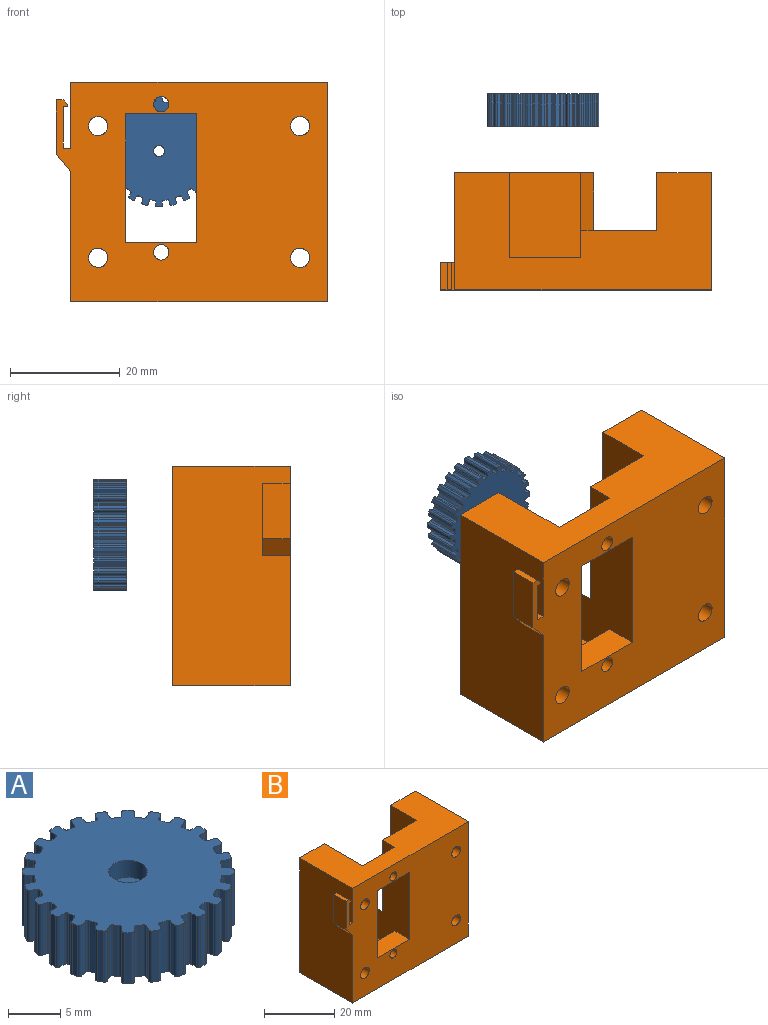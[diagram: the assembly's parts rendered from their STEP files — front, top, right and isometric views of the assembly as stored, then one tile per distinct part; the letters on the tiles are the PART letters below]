
ASSEMBLY  parts=2 mates=1
PART A: 197 faces, bbox 20.4x20.4x6 mm
  f0: cylinder r=1mm len=4mm, axis (0,0,1), area 25.1mm2, adj f194,f196
  f1: cylinder r=0.3mm len=6mm, axis (0,0,-1), area 2.7mm2, adj f2,f192,f193,f194
  f2: cylinder r=9mm len=6mm, axis (0,0,-1), area 3.7mm2, adj f1,f3,f193,f194
  f3: cylinder r=0.3mm len=6mm, axis (0,0,-1), area 2.7mm2, adj f2,f4,f193,f194
  f4: plane 6x0.54mm, normal (0.5,-0.87,0), area 3.7mm2, adj f3,f5,f193,f194
  f5: cylinder r=0.3mm len=6mm, axis (0,0,-1), area 2.8mm2, adj f4,f6,f193,f194
  f6: plane 6x0.52mm, normal (0.87,0.5,0), area 3.6mm2, adj f5,f7,f193,f194
  f7: cylinder r=0.3mm len=6mm, axis (0,0,-1), area 2.8mm2, adj f6,f8,f193,f194
  f8: plane 6x0.54mm, normal (-0.5,0.87,0), area 3.7mm2, adj f7,f9,f193,f194
  f9: cylinder r=0.3mm len=6mm, axis (0,0,-1), area 2.7mm2, adj f8,f10,f193,f194
  f10: cylinder r=9mm len=6mm, axis (0,0,-1), area 3.7mm2, adj f9,f11,f193,f194
  f11: cylinder r=0.3mm len=6mm, axis (0,0,-1), area 2.7mm2, adj f10,f12,f193,f194
  f12: plane 6x0.44mm, normal (0.71,-0.71,0), area 3.7mm2, adj f11,f13,f193,f194
  f13: cylinder r=0.3mm len=6mm, axis (0,0,-1), area 2.8mm2, adj f12,f14,f193,f194
  f14: plane 6x0.42mm, normal (0.71,0.71,0), area 3.6mm2, adj f13,f15,f193,f194
  f15: cylinder r=0.3mm len=6mm, axis (0,0,-1), area 2.8mm2, adj f14,f16,f193,f194
  f16: plane 6x0.44mm, normal (-0.71,0.71,0), area 3.7mm2, adj f15,f17,f193,f194
  f17: cylinder r=0.3mm len=6mm, axis (0,0,-1), area 2.7mm2, adj f16,f18,f193,f194
  f18: cylinder r=9mm len=6mm, axis (0,0,-1), area 3.7mm2, adj f17,f19,f193,f194
  f19: cylinder r=0.3mm len=6mm, axis (0,0,-1), area 2.7mm2, adj f18,f20,f193,f194
  f20: plane 6x0.54mm, normal (0.87,-0.5,0), area 3.7mm2, adj f19,f21,f193,f194
  f21: cylinder r=0.3mm len=6mm, axis (0,0,-1), area 2.8mm2, adj f20,f22,f193,f194
  f22: plane 6x0.52mm, normal (0.5,0.87,0), area 3.6mm2, adj f21,f23,f193,f194
  f23: cylinder r=0.3mm len=6mm, axis (0,0,-1), area 2.8mm2, adj f22,f24,f193,f194
  f24: plane 6x0.54mm, normal (-0.87,0.5,0), area 3.7mm2, adj f23,f25,f193,f194
  f25: cylinder r=0.3mm len=6mm, axis (0,0,-1), area 2.7mm2, adj f24,f26,f193,f194
  f26: cylinder r=9mm len=6mm, axis (0,0,-1), area 3.7mm2, adj f25,f27,f193,f194
  f27: cylinder r=0.3mm len=6mm, axis (0,0,-1), area 2.7mm2, adj f26,f28,f193,f194
  f28: plane 6x0.6mm, normal (0.97,-0.26,0), area 3.7mm2, adj f27,f29,f193,f194
  f29: cylinder r=0.3mm len=6mm, axis (0,0,-1), area 2.8mm2, adj f28,f30,f193,f194
  f30: plane 6x0.58mm, normal (0.26,0.97,0), area 3.6mm2, adj f29,f31,f193,f194
  f31: cylinder r=0.3mm len=6mm, axis (0,0,-1), area 2.8mm2, adj f30,f32,f193,f194
  f32: plane 6x0.6mm, normal (-0.97,0.26,0), area 3.7mm2, adj f31,f33,f193,f194
  f33: cylinder r=0.3mm len=6mm, axis (0,0,-1), area 2.7mm2, adj f32,f34,f193,f194
  f34: cylinder r=9mm len=6mm, axis (0,0,-1), area 3.7mm2, adj f33,f35,f193,f194
  f35: cylinder r=0.3mm len=6mm, axis (0,0,-1), area 2.7mm2, adj f34,f36,f193,f194
  f36: plane 6x0.62mm, normal (1,0,0), area 3.7mm2, adj f35,f37,f193,f194
  f37: cylinder r=0.3mm len=6mm, axis (0,0,-1), area 2.8mm2, adj f36,f38,f193,f194
  f38: plane 6x0.6mm, normal (0,1,0), area 3.6mm2, adj f37,f39,f193,f194
  f39: cylinder r=0.3mm len=6mm, axis (0,0,-1), area 2.8mm2, adj f38,f40,f193,f194
  f40: plane 6x0.62mm, normal (-1,0,0), area 3.7mm2, adj f39,f41,f193,f194
  f41: cylinder r=0.3mm len=6mm, axis (0,0,-1), area 2.7mm2, adj f40,f42,f193,f194
  f42: cylinder r=9mm len=6mm, axis (0,0,-1), area 3.7mm2, adj f41,f43,f193,f194
  f43: cylinder r=0.3mm len=6mm, axis (0,0,-1), area 2.7mm2, adj f42,f44,f193,f194
  f44: plane 6x0.6mm, normal (0.97,0.26,0), area 3.7mm2, adj f43,f45,f193,f194
  f45: cylinder r=0.3mm len=6mm, axis (0,0,-1), area 2.8mm2, adj f44,f46,f193,f194
  f46: plane 6x0.58mm, normal (-0.26,0.97,0), area 3.6mm2, adj f45,f47,f193,f194
  f47: cylinder r=0.3mm len=6mm, axis (0,0,-1), area 2.8mm2, adj f46,f48,f193,f194
  f48: plane 6x0.6mm, normal (-0.97,-0.26,0), area 3.7mm2, adj f47,f49,f193,f194
  f49: cylinder r=0.3mm len=6mm, axis (0,0,-1), area 2.7mm2, adj f48,f50,f193,f194
  f50: cylinder r=9mm len=6mm, axis (0,0,-1), area 3.7mm2, adj f49,f51,f193,f194
  f51: cylinder r=0.3mm len=6mm, axis (0,0,-1), area 2.7mm2, adj f50,f52,f193,f194
  f52: plane 6x0.54mm, normal (0.87,0.5,0), area 3.7mm2, adj f51,f53,f193,f194
  f53: cylinder r=0.3mm len=6mm, axis (0,0,-1), area 2.8mm2, adj f52,f54,f193,f194
  f54: plane 6x0.52mm, normal (-0.5,0.87,0), area 3.6mm2, adj f53,f55,f193,f194
  f55: cylinder r=0.3mm len=6mm, axis (0,0,-1), area 2.8mm2, adj f54,f56,f193,f194
  f56: plane 6x0.54mm, normal (-0.87,-0.5,0), area 3.7mm2, adj f55,f57,f193,f194
  f57: cylinder r=0.3mm len=6mm, axis (0,0,-1), area 2.7mm2, adj f56,f58,f193,f194
  f58: cylinder r=9mm len=6mm, axis (0,0,-1), area 3.7mm2, adj f57,f59,f193,f194
  f59: cylinder r=0.3mm len=6mm, axis (0,0,-1), area 2.7mm2, adj f58,f60,f193,f194
  f60: plane 6x0.44mm, normal (0.71,0.71,0), area 3.7mm2, adj f59,f61,f193,f194
  f61: cylinder r=0.3mm len=6mm, axis (0,0,-1), area 2.8mm2, adj f60,f62,f193,f194
  f62: plane 6x0.42mm, normal (-0.71,0.71,0), area 3.6mm2, adj f61,f63,f193,f194
  f63: cylinder r=0.3mm len=6mm, axis (0,0,-1), area 2.8mm2, adj f62,f64,f193,f194
  f64: plane 6x0.44mm, normal (-0.71,-0.71,0), area 3.7mm2, adj f63,f65,f193,f194
  f65: cylinder r=0.3mm len=6mm, axis (0,0,-1), area 2.7mm2, adj f64,f66,f193,f194
  f66: cylinder r=9mm len=6mm, axis (0,0,-1), area 3.7mm2, adj f65,f67,f193,f194
  f67: cylinder r=0.3mm len=6mm, axis (0,0,-1), area 2.7mm2, adj f66,f68,f193,f194
  f68: plane 6x0.54mm, normal (0.5,0.87,0), area 3.7mm2, adj f67,f69,f193,f194
  f69: cylinder r=0.3mm len=6mm, axis (0,0,-1), area 2.8mm2, adj f68,f70,f193,f194
  f70: plane 6x0.52mm, normal (-0.87,0.5,0), area 3.6mm2, adj f69,f71,f193,f194
  f71: cylinder r=0.3mm len=6mm, axis (0,0,-1), area 2.8mm2, adj f70,f72,f193,f194
  f72: plane 6x0.54mm, normal (-0.5,-0.87,0), area 3.7mm2, adj f71,f73,f193,f194
  f73: cylinder r=0.3mm len=6mm, axis (0,0,-1), area 2.7mm2, adj f72,f74,f193,f194
  f74: cylinder r=9mm len=6mm, axis (0,0,-1), area 3.7mm2, adj f73,f75,f193,f194
  f75: cylinder r=0.3mm len=6mm, axis (0,0,-1), area 2.7mm2, adj f74,f76,f193,f194
  f76: plane 6x0.6mm, normal (0.26,0.97,0), area 3.7mm2, adj f75,f77,f193,f194
  f77: cylinder r=0.3mm len=6mm, axis (0,0,-1), area 2.8mm2, adj f76,f78,f193,f194
  f78: plane 6x0.58mm, normal (-0.97,0.26,0), area 3.6mm2, adj f77,f79,f193,f194
  f79: cylinder r=0.3mm len=6mm, axis (0,0,-1), area 2.8mm2, adj f78,f80,f193,f194
  f80: plane 6x0.6mm, normal (-0.26,-0.97,0), area 3.7mm2, adj f79,f81,f193,f194
  f81: cylinder r=0.3mm len=6mm, axis (0,0,-1), area 2.7mm2, adj f80,f82,f193,f194
  f82: cylinder r=9mm len=6mm, axis (0,0,-1), area 3.7mm2, adj f81,f83,f193,f194
  f83: cylinder r=0.3mm len=6mm, axis (0,0,-1), area 2.7mm2, adj f82,f84,f193,f194
  f84: plane 6x0.62mm, normal (0,1,0), area 3.7mm2, adj f83,f85,f193,f194
  f85: cylinder r=0.3mm len=6mm, axis (0,0,-1), area 2.8mm2, adj f84,f86,f193,f194
  f86: plane 6x0.6mm, normal (-1,0,0), area 3.6mm2, adj f85,f87,f193,f194
  f87: cylinder r=0.3mm len=6mm, axis (0,0,-1), area 2.8mm2, adj f86,f88,f193,f194
  f88: plane 6x0.62mm, normal (0,-1,0), area 3.7mm2, adj f87,f89,f193,f194
  f89: cylinder r=0.3mm len=6mm, axis (0,0,-1), area 2.7mm2, adj f88,f90,f193,f194
  f90: cylinder r=9mm len=6mm, axis (0,0,-1), area 3.7mm2, adj f89,f91,f193,f194
  f91: cylinder r=0.3mm len=6mm, axis (0,0,-1), area 2.7mm2, adj f90,f92,f193,f194
  f92: plane 6x0.6mm, normal (-0.26,0.97,0), area 3.7mm2, adj f91,f93,f193,f194
  f93: cylinder r=0.3mm len=6mm, axis (0,0,-1), area 2.8mm2, adj f92,f94,f193,f194
  f94: plane 6x0.58mm, normal (-0.97,-0.26,0), area 3.6mm2, adj f93,f95,f193,f194
  f95: cylinder r=0.3mm len=6mm, axis (0,0,-1), area 2.8mm2, adj f94,f96,f193,f194
  f96: plane 6x0.6mm, normal (0.26,-0.97,0), area 3.7mm2, adj f95,f97,f193,f194
  f97: cylinder r=0.3mm len=6mm, axis (0,0,-1), area 2.7mm2, adj f96,f98,f193,f194
  f98: cylinder r=9mm len=6mm, axis (0,0,-1), area 3.7mm2, adj f97,f99,f193,f194
  f99: cylinder r=0.3mm len=6mm, axis (0,0,-1), area 2.7mm2, adj f98,f100,f193,f194
  f100: plane 6x0.54mm, normal (-0.5,0.87,0), area 3.7mm2, adj f99,f101,f193,f194
  f101: cylinder r=0.3mm len=6mm, axis (0,0,-1), area 2.8mm2, adj f100,f102,f193,f194
  f102: plane 6x0.52mm, normal (-0.87,-0.5,0), area 3.6mm2, adj f101,f103,f193,f194
  f103: cylinder r=0.3mm len=6mm, axis (0,0,-1), area 2.8mm2, adj f102,f104,f193,f194
  f104: plane 6x0.54mm, normal (0.5,-0.87,0), area 3.7mm2, adj f103,f105,f193,f194
  f105: cylinder r=0.3mm len=6mm, axis (0,0,-1), area 2.7mm2, adj f104,f106,f193,f194
  f106: cylinder r=9mm len=6mm, axis (0,0,-1), area 3.7mm2, adj f105,f107,f193,f194
  f107: cylinder r=0.3mm len=6mm, axis (0,0,-1), area 2.7mm2, adj f106,f108,f193,f194
  f108: plane 6x0.44mm, normal (-0.71,0.71,0), area 3.7mm2, adj f107,f109,f193,f194
  f109: cylinder r=0.3mm len=6mm, axis (0,0,-1), area 2.8mm2, adj f108,f110,f193,f194
  f110: plane 6x0.42mm, normal (-0.71,-0.71,0), area 3.6mm2, adj f109,f111,f193,f194
  f111: cylinder r=0.3mm len=6mm, axis (0,0,-1), area 2.8mm2, adj f110,f112,f193,f194
  f112: plane 6x0.44mm, normal (0.71,-0.71,0), area 3.7mm2, adj f111,f113,f193,f194
  f113: cylinder r=0.3mm len=6mm, axis (0,0,-1), area 2.7mm2, adj f112,f114,f193,f194
  f114: cylinder r=9mm len=6mm, axis (0,0,-1), area 3.7mm2, adj f113,f115,f193,f194
  f115: cylinder r=0.3mm len=6mm, axis (0,0,-1), area 2.7mm2, adj f114,f116,f193,f194
  f116: plane 6x0.54mm, normal (-0.87,0.5,0), area 3.7mm2, adj f115,f117,f193,f194
  f117: cylinder r=0.3mm len=6mm, axis (0,0,-1), area 2.8mm2, adj f116,f118,f193,f194
  f118: plane 6x0.52mm, normal (-0.5,-0.87,0), area 3.6mm2, adj f117,f119,f193,f194
  f119: cylinder r=0.3mm len=6mm, axis (0,0,-1), area 2.8mm2, adj f118,f120,f193,f194
  f120: plane 6x0.54mm, normal (0.87,-0.5,0), area 3.7mm2, adj f119,f121,f193,f194
  f121: cylinder r=0.3mm len=6mm, axis (0,0,-1), area 2.7mm2, adj f120,f122,f193,f194
  f122: cylinder r=9mm len=6mm, axis (0,0,-1), area 3.7mm2, adj f121,f123,f193,f194
  f123: cylinder r=0.3mm len=6mm, axis (0,0,-1), area 2.7mm2, adj f122,f124,f193,f194
  f124: plane 6x0.6mm, normal (-0.97,0.26,0), area 3.7mm2, adj f123,f125,f193,f194
  f125: cylinder r=0.3mm len=6mm, axis (0,0,-1), area 2.8mm2, adj f124,f126,f193,f194
  f126: plane 6x0.58mm, normal (-0.26,-0.97,0), area 3.6mm2, adj f125,f127,f193,f194
  f127: cylinder r=0.3mm len=6mm, axis (0,0,-1), area 2.8mm2, adj f126,f128,f193,f194
  f128: plane 6x0.6mm, normal (0.97,-0.26,0), area 3.7mm2, adj f127,f129,f193,f194
  f129: cylinder r=0.3mm len=6mm, axis (0,0,-1), area 2.7mm2, adj f128,f130,f193,f194
  f130: cylinder r=9mm len=6mm, axis (0,0,-1), area 3.7mm2, adj f129,f131,f193,f194
  f131: cylinder r=0.3mm len=6mm, axis (0,0,-1), area 2.7mm2, adj f130,f132,f193,f194
  f132: plane 6x0.62mm, normal (-1,0,0), area 3.7mm2, adj f131,f133,f193,f194
  f133: cylinder r=0.3mm len=6mm, axis (0,0,-1), area 2.8mm2, adj f132,f134,f193,f194
  f134: plane 6x0.6mm, normal (0,-1,0), area 3.6mm2, adj f133,f135,f193,f194
  f135: cylinder r=0.3mm len=6mm, axis (0,0,-1), area 2.8mm2, adj f134,f136,f193,f194
  f136: plane 6x0.62mm, normal (1,0,0), area 3.7mm2, adj f135,f137,f193,f194
  f137: cylinder r=0.3mm len=6mm, axis (0,0,-1), area 2.7mm2, adj f136,f138,f193,f194
  f138: cylinder r=9mm len=6mm, axis (0,0,-1), area 3.7mm2, adj f137,f139,f193,f194
  f139: cylinder r=0.3mm len=6mm, axis (0,0,-1), area 2.7mm2, adj f138,f140,f193,f194
  f140: plane 6x0.6mm, normal (-0.97,-0.26,0), area 3.7mm2, adj f139,f141,f193,f194
  f141: cylinder r=0.3mm len=6mm, axis (0,0,-1), area 2.8mm2, adj f140,f142,f193,f194
  f142: plane 6x0.58mm, normal (0.26,-0.97,0), area 3.6mm2, adj f141,f143,f193,f194
  f143: cylinder r=0.3mm len=6mm, axis (0,0,-1), area 2.8mm2, adj f142,f144,f193,f194
  f144: plane 6x0.6mm, normal (0.97,0.26,0), area 3.7mm2, adj f143,f145,f193,f194
  f145: cylinder r=0.3mm len=6mm, axis (0,0,-1), area 2.7mm2, adj f144,f146,f193,f194
  f146: cylinder r=9mm len=6mm, axis (0,0,-1), area 3.7mm2, adj f145,f147,f193,f194
  f147: cylinder r=0.3mm len=6mm, axis (0,0,-1), area 2.7mm2, adj f146,f148,f193,f194
  f148: plane 6x0.54mm, normal (-0.87,-0.5,0), area 3.7mm2, adj f147,f149,f193,f194
  f149: cylinder r=0.3mm len=6mm, axis (0,0,-1), area 2.8mm2, adj f148,f150,f193,f194
  f150: plane 6x0.52mm, normal (0.5,-0.87,0), area 3.6mm2, adj f149,f151,f193,f194
  f151: cylinder r=0.3mm len=6mm, axis (0,0,-1), area 2.8mm2, adj f150,f152,f193,f194
  f152: plane 6x0.54mm, normal (0.87,0.5,0), area 3.7mm2, adj f151,f153,f193,f194
  f153: cylinder r=0.3mm len=6mm, axis (0,0,-1), area 2.7mm2, adj f152,f154,f193,f194
  f154: cylinder r=9mm len=6mm, axis (0,0,-1), area 3.7mm2, adj f153,f155,f193,f194
  f155: cylinder r=0.3mm len=6mm, axis (0,0,-1), area 2.7mm2, adj f154,f156,f193,f194
  f156: plane 6x0.44mm, normal (-0.71,-0.71,0), area 3.7mm2, adj f155,f157,f193,f194
  f157: cylinder r=0.3mm len=6mm, axis (0,0,-1), area 2.8mm2, adj f156,f158,f193,f194
  f158: plane 6x0.42mm, normal (0.71,-0.71,0), area 3.6mm2, adj f157,f159,f193,f194
  f159: cylinder r=0.3mm len=6mm, axis (0,0,-1), area 2.8mm2, adj f158,f160,f193,f194
  f160: plane 6x0.44mm, normal (0.71,0.71,0), area 3.7mm2, adj f159,f161,f193,f194
  f161: cylinder r=0.3mm len=6mm, axis (0,0,-1), area 2.7mm2, adj f160,f162,f193,f194
  f162: cylinder r=9mm len=6mm, axis (0,0,-1), area 3.7mm2, adj f161,f163,f193,f194
  f163: cylinder r=0.3mm len=6mm, axis (0,0,-1), area 2.7mm2, adj f162,f164,f193,f194
  f164: plane 6x0.54mm, normal (-0.5,-0.87,0), area 3.7mm2, adj f163,f165,f193,f194
  f165: cylinder r=0.3mm len=6mm, axis (0,0,-1), area 2.8mm2, adj f164,f166,f193,f194
  f166: plane 6x0.52mm, normal (0.87,-0.5,0), area 3.6mm2, adj f165,f167,f193,f194
  f167: cylinder r=0.3mm len=6mm, axis (0,0,-1), area 2.8mm2, adj f166,f168,f193,f194
  f168: plane 6x0.54mm, normal (0.5,0.87,0), area 3.7mm2, adj f167,f169,f193,f194
  f169: cylinder r=0.3mm len=6mm, axis (0,0,-1), area 2.7mm2, adj f168,f170,f193,f194
  f170: cylinder r=9mm len=6mm, axis (0,0,-1), area 3.7mm2, adj f169,f171,f193,f194
  f171: cylinder r=0.3mm len=6mm, axis (0,0,-1), area 2.7mm2, adj f170,f172,f193,f194
  f172: plane 6x0.6mm, normal (-0.26,-0.97,0), area 3.7mm2, adj f171,f173,f193,f194
  f173: cylinder r=0.3mm len=6mm, axis (0,0,-1), area 2.8mm2, adj f172,f174,f193,f194
  f174: plane 6x0.58mm, normal (0.97,-0.26,0), area 3.6mm2, adj f173,f175,f193,f194
  f175: cylinder r=0.3mm len=6mm, axis (0,0,-1), area 2.8mm2, adj f174,f176,f193,f194
  f176: plane 6x0.6mm, normal (0.26,0.97,0), area 3.7mm2, adj f175,f177,f193,f194
  f177: cylinder r=0.3mm len=6mm, axis (0,0,-1), area 2.7mm2, adj f176,f178,f193,f194
  f178: cylinder r=9mm len=6mm, axis (0,0,-1), area 3.7mm2, adj f177,f179,f193,f194
  f179: cylinder r=0.3mm len=6mm, axis (0,0,-1), area 2.7mm2, adj f178,f180,f193,f194
  f180: plane 6x0.62mm, normal (0,-1,0), area 3.7mm2, adj f179,f181,f193,f194
  f181: cylinder r=0.3mm len=6mm, axis (0,0,-1), area 2.8mm2, adj f180,f182,f193,f194
  f182: plane 6x0.6mm, normal (1,0,0), area 3.6mm2, adj f181,f183,f193,f194
  f183: cylinder r=0.3mm len=6mm, axis (0,0,-1), area 2.8mm2, adj f182,f184,f193,f194
  f184: plane 6x0.62mm, normal (0,1,0), area 3.7mm2, adj f183,f185,f193,f194
  f185: cylinder r=0.3mm len=6mm, axis (0,0,-1), area 2.7mm2, adj f184,f186,f193,f194
  f186: cylinder r=9mm len=6mm, axis (0,0,-1), area 3.7mm2, adj f185,f187,f193,f194
  f187: cylinder r=0.3mm len=6mm, axis (0,0,-1), area 2.7mm2, adj f186,f188,f193,f194
  f188: plane 6x0.6mm, normal (0.26,-0.97,0), area 3.7mm2, adj f187,f189,f193,f194
  f189: cylinder r=0.3mm len=6mm, axis (0,0,-1), area 2.8mm2, adj f188,f190,f193,f194
  f190: plane 6x0.58mm, normal (0.97,0.26,0), area 3.6mm2, adj f189,f191,f193,f194
  f191: cylinder r=0.3mm len=6mm, axis (0,0,-1), area 2.8mm2, adj f190,f192,f193,f194
  f192: plane 6x0.6mm, normal (-0.26,0.97,0), area 3.7mm2, adj f1,f191,f193,f194
  f193: plane 20.36x20.36mm, normal (0,0,1), area 277.7mm2, adj f1,f2,f3,f4,f5,f6,f7,f8
  f194: plane 20.36x20.36mm, normal (0,0,-1), area 285.3mm2, adj f0,f1,f2,f3,f4,f5,f6,f7
  f195: cylinder r=1.85mm len=3.7mm, axis (0,0,1), area 23.2mm2, adj f193,f196
  f196: plane 3.7x3.7mm, normal (0,0,1), area 7.6mm2, adj f0,f195
PART B: 41 faces, bbox 49.4x21.4x40 mm
  f0: cylinder r=1.75mm len=15.39mm, axis (0,1,0), area 169.2mm2, adj f6,f39
  f1: cylinder r=1.75mm len=15.39mm, axis (0,1,0), area 169.2mm2, adj f6,f37
  f2: cylinder r=1.75mm len=15.39mm, axis (0,1,0), area 169.2mm2, adj f6,f35
  f3: cylinder r=1.75mm len=15.39mm, axis (0,1,0), area 169.2mm2, adj f6,f33
  f4: plane 40x10mm, normal (0,1,0), area 299.5mm2, adj f8,f12,f13,f22,f34,f36
  f5: plane 13x5.75mm, normal (0,1,0), area 68.6mm2, adj f8,f10,f15,f17,f20
  f6: plane 49.4x40mm, normal (0,-1,0), area 1534mm2, adj f0,f1,f2,f3,f8,f9,f10,f12
  f7: plane 40x13.8mm, normal (0,1,0), area 522.1mm2, adj f8,f12,f13,f14,f16,f17
  f8: plane 46.8x21.39mm, normal (0,0,1), area 654.7mm2, adj f4,f5,f6,f7,f11,f13,f15,f17
  f9: cylinder r=1.4mm len=5.89mm, axis (0,1,0), area 51.8mm2, adj f6,f19
  f10: cylinder r=1.4mm len=5.89mm, axis (0,1,0), area 51.8mm2, adj f5,f6
  f11: plane 40x25.3mm, normal (0,1,0), area 394.4mm2, adj f8,f12,f14,f15,f16,f17,f18,f23
  f12: plane 46.8x21.39mm, normal (0,0,-1), area 880.3mm2, adj f4,f6,f7,f11,f13,f14,f22,f23
  f13: plane 40x10.5mm, normal (-1,0,0), area 420mm2, adj f4,f7,f8,f12
  f14: plane 11x10.5mm, normal (1,0,0), area 115.5mm2, adj f7,f11,f12,f16
  f15: plane 35x21.39mm, normal (1,0,0), area 680.9mm2, adj f5,f6,f8,f11,f18,f19,f20,f21
  f16: plane 10.5x4mm, normal (0.87,0,0.5), area 48.4mm2, adj f7,f11,f14,f17
  f17: plane 35x21.39mm, normal (-1,0,0), area 418.4mm2, adj f5,f6,f7,f8,f11,f16,f18,f19
  f18: plane 15.5x13mm, normal (0,0,1), area 201.5mm2, adj f11,f15,f17,f19
  f19: plane 13x5.75mm, normal (0,1,0), area 68.6mm2, adj f9,f15,f17,f18,f21
  f20: plane 13x5.89mm, normal (0,0,-1), area 76.6mm2, adj f5,f6,f15,f17
  f21: plane 13x5.89mm, normal (0,0,1), area 76.6mm2, adj f6,f15,f17,f19
  f22: plane 40x21.39mm, normal (1,0,0), area 855.6mm2, adj f4,f6,f8,f12
  f23: plane 40x21.39mm, normal (-1,0,0), area 834.1mm2, adj f6,f8,f11,f12,f24,f30,f31
  f24: plane 5x1.4mm, normal (0,0,1), area 7mm2, adj f6,f23,f25,f31
  f25: plane 7.6x5mm, normal (1,0,0), area 38mm2, adj f6,f24,f26,f31
  f26: plane 5x0.8mm, normal (0,0,-1), area 4mm2, adj f6,f25,f27,f31
  f27: plane 5x0.4mm, normal (1,0,0), area 2mm2, adj f6,f26,f31,f32
  f28: plane 5x1.2mm, normal (0,0,1), area 6mm2, adj f6,f29,f31,f32
  f29: plane 10x5mm, normal (-1,0,0), area 50mm2, adj f6,f28,f30,f31
  f30: plane 5x3.1mm, normal (-0.77,0,-0.64), area 20.2mm2, adj f6,f23,f29,f31
  f31: plane 13.1x2.6mm, normal (0,1,0), area 18.3mm2, adj f23,f24,f25,f26,f27,f28,f29,f30
  f32: plane 5x0.8mm, normal (0.71,0,0.71), area 5.7mm2, adj f6,f27,f28,f31
  f33: plane 8x8mm, normal (0,1,0), area 40.6mm2, adj f3,f34
  f34: cylinder r=4mm len=8mm, axis (0,1,0), area 150.8mm2, adj f4,f33
  f35: plane 8x8mm, normal (0,1,0), area 40.6mm2, adj f2,f36
  f36: cylinder r=4mm len=8mm, axis (0,1,0), area 150.8mm2, adj f4,f35
  f37: plane 8x8mm, normal (0,1,0), area 40.6mm2, adj f1,f38
  f38: cylinder r=4mm len=8mm, axis (0,1,0), area 150.8mm2, adj f11,f37
  f39: plane 8x8mm, normal (0,1,0), area 40.6mm2, adj f0,f40
  f40: cylinder r=4mm len=8mm, axis (0,1,0), area 150.8mm2, adj f11,f39
PLACE A rot(axis=(-0.58,-0.58,-0.58),120deg) t=(-20.01,19.69,15.45)mm
PLACE B t=(-20.56,2.39,-12)mm
MATE parallel A.f0 <-> B.f4  axis (0,-1,0) through (-20.01,19.69,15.45)mm
